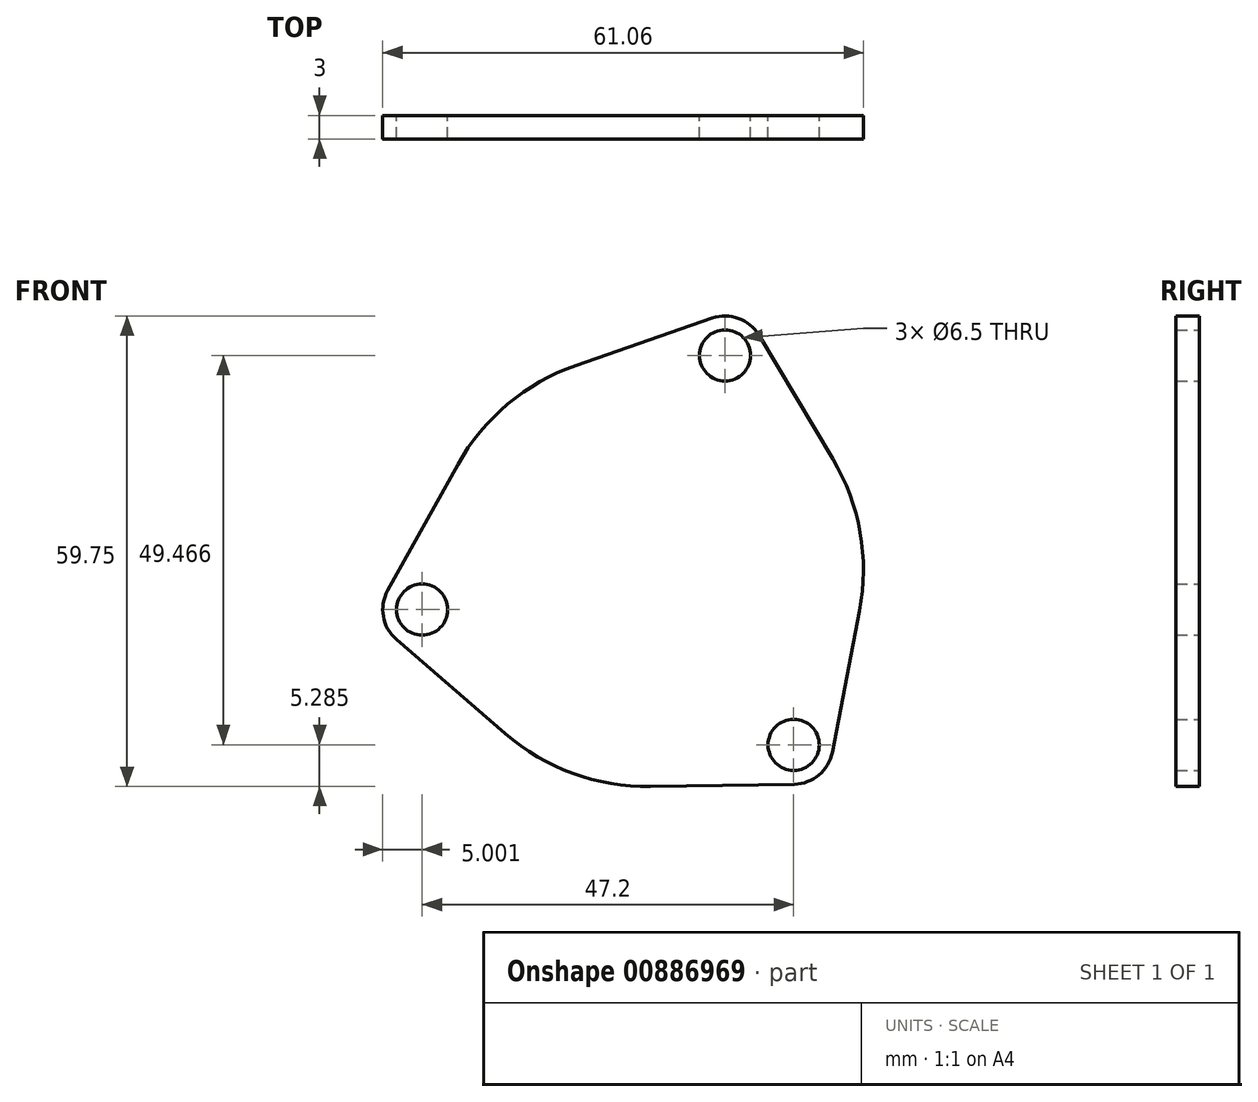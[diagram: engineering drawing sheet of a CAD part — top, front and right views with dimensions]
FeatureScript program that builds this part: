
annotation { "Feature Type Name" : "Feature", "Feature Type Description" : "" }
export const myFeature = defineFeature(function(context is Context, id is Id, definition is map)
    precondition{}
    {
        {
            var Q0;
            Q0=qCreatedBy(makeId("Front.planeOp"),FACE);
            var sketch = newSketch(context, id + "F0", { "sketchPlane" : qUnion([Q0])});
            skArc(sketch, "E0", {"start": v(-9, 25.98) * mm, "mid": v(-17.68, 21.07) * mm, "end": v(-24.02, 13.38) * mm});
            skLineSegment(sketch, "E1", {"start": v(0, 0) * mm, "end": v(0, 34.88) * mm, "construction": true});
            skLineSegment(sketch, "E2", {"start": v(0, 0) * mm, "end": v(9.92, 27.25) * mm, "construction": true});
            skArc(sketch, "E3", {"start": v(14.2, 29.82) * mm, "mid": v(11.63, 31.95) * mm, "end": v(8.28, 31.98) * mm});
            skCircle(sketch, "E4", {"center": v(9.92, 27.25) * mm, "radius": 3.25 * mm});
            skLineSegment(sketch, "E5", {"start": v(14.2, 29.82) * mm, "end": v(23.6, 14.12) * mm});
            skLineSegment(sketch, "E6.MirrorCS", {"start": v(8.28, 31.98) * mm, "end": v(-9, 25.98) * mm});
            skLineSegment(sketch, "E7.1.0", {"start": v(-32.93, -2.6) * mm, "end": v(-24.02, 13.38) * mm});
            skArc(sketch, "E7.1.1", {"start": v(-32.93, -2.6) * mm, "mid": v(-33.48, -5.9) * mm, "end": v(-31.83, -8.82) * mm});
            skLineSegment(sketch, "E7.1.2", {"start": v(-31.83, -8.82) * mm, "end": v(-18, -20.8) * mm});
            skCircle(sketch, "E7.1.3", {"center": v(-28.56, -5.04) * mm, "radius": 3.25 * mm});
            skLineSegment(sketch, "E7.2.0", {"start": v(18.72, -27.21) * mm, "end": v(0.42, -27.5) * mm});
            skArc(sketch, "E7.2.1", {"start": v(18.72, -27.21) * mm, "mid": v(21.85, -26.05) * mm, "end": v(23.55, -23.16) * mm});
            skLineSegment(sketch, "E7.2.2", {"start": v(23.55, -23.16) * mm, "end": v(27, -5.2) * mm});
            skCircle(sketch, "E7.2.3", {"center": v(18.64, -22.22) * mm, "radius": 3.25 * mm});
            skArc(sketch, "E8.trimOffspring", {"start": v(-18, -20.8) * mm, "mid": v(-9.4, -25.84) * mm, "end": v(0.42, -27.5) * mm});
            skArc(sketch, "E9.trimOffspring", {"start": v(27, -5.2) * mm, "mid": v(27.08, 4.78) * mm, "end": v(23.6, 14.12) * mm});
            skSolve(sketch);
        }
        {
            var Q0;
            Q0 = qSketchRegion(id + "F0", true);
            extrude(context, id + "F1", {"entities" : qUnion([Q0]), "depth" : 3 * mm, "offsetDistance" : 25 * mm});
        }
    });
